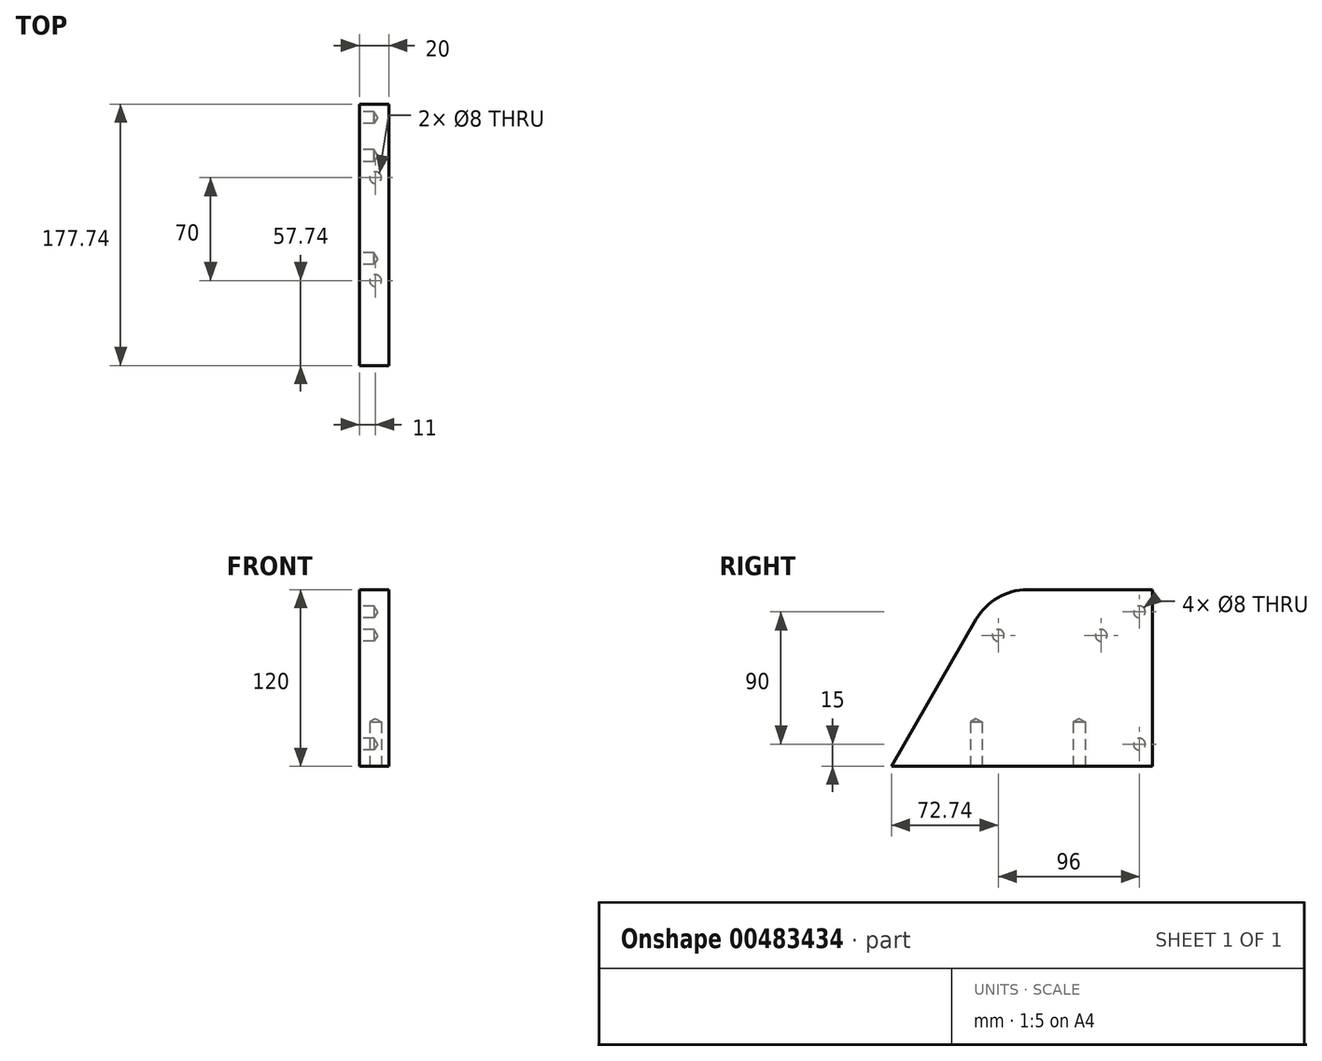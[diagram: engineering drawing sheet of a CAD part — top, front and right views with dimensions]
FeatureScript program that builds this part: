
annotation { "Feature Type Name" : "Feature", "Feature Type Description" : "" }
export const myFeature = defineFeature(function(context is Context, id is Id, definition is map)
    precondition{}
    {
        {
            var Q0;
            Q0=qCreatedBy(makeId("Right.planeOp"),FACE);
            var sketch = newSketch(context, id + "F0", { "sketchPlane" : qUnion([Q0])});
            skLineSegment(sketch, "E0", {"start": v(0, 0) * mm, "end": v(-177.74, 0) * mm});
            skLineSegment(sketch, "E1", {"start": v(-177.74, 0) * mm, "end": v(-120, 100) * mm});
            skLineSegment(sketch, "E2", {"start": v(-108.45, 120) * mm, "end": v(0, 120) * mm});
            skPoint(sketch, "E3", {"position": v(0, 100) * mm});
            skLineSegment(sketch, "E4", {"start": v(0, 100) * mm, "end": v(0, 120) * mm});
            skLineSegment(sketch, "E5", {"start": v(0, 100) * mm, "end": v(0, 0) * mm});
            skLineSegment(sketch, "E6", {"start": v(-120, 100) * mm, "end": v(-108.45, 120) * mm});
            skLineSegment(sketch, "E7", {"start": v(0, 100) * mm, "end": v(-120, 100) * mm});
            skSolve(sketch);
        }
        {
            var Q0;
            Q0=qSketchRegion(id+"F0",true);
            extrude(context, id + "F1", {"entities" : qUnion([Q0]), "depth" : 20 * mm});
        }
        {
            var Q0;
            Q0=makeQuery(id+"F1.opExtrude","SWEPT_EDGE",EDGE,{"disambiguationData":[OSD([sQuery(id+"F0.wireOp",EDGE,"E2"),sQuery(id+"F0.wireOp",EDGE,"E6")])]});
            fillet(context, id + "F2", {"entities" : qUnion([Q0]), "radius" : 40 * mm, "tangentPropagation" : true, "allowEdgeOverflow" : false});
        }
        {
            var Q0;
            Q0=makeQuery(id+"F1.opExtrude","CAP_FACE",FACE,{"disambiguationData":[OSD([sQuery(id+"F0.wireOp",EDGE,"E0"),sQuery(id+"F0.wireOp",EDGE,"E1"),sQuery(id+"F0.wireOp",EDGE,"E2"),sQuery(id+"F0.wireOp",EDGE,"E4"),sQuery(id+"F0.wireOp",EDGE,"E5"),sQuery(id+"F0.wireOp",EDGE,"E6")])],"isStart":true});
            var sketch = newSketch(context, id + "F3", { "sketchPlane" : qUnion([Q0])});
            skPoint(sketch, "E8", {"position": v(35, 89) * mm});
            skPoint(sketch, "E9", {"position": v(105, 89) * mm});
            skPoint(sketch, "E10", {"position": v(9, 15) * mm});
            skPoint(sketch, "E11", {"position": v(9, 105) * mm});
            skSolve(sketch);
        }
        {
            var Q0;
            Q0=makeQuery(id+"F1.opExtrude","SWEPT_FACE",FACE,{"disambiguationData":[OSD([sQuery(id+"F0.wireOp",EDGE,"E0")])]});
            var sketch = newSketch(context, id + "F4", { "sketchPlane" : qUnion([Q0])});
            skPoint(sketch, "E12", {"position": v(11, 50) * mm});
            skPoint(sketch, "E13", {"position": v(11, 120) * mm});
            skSolve(sketch);
        }
        {
            var Q0;
            Q0=sQuery(id+"F3.wireOp",VERTEX,"E8");
            var Q1;
            Q1=sQuery(id+"F3.wireOp",VERTEX,"E9");
            var Q2;
            Q2=sQuery(id+"F3.wireOp",VERTEX,"E10");
            var Q3;
            Q3=sQuery(id+"F3.wireOp",VERTEX,"E11");
            var Q4;
            Q4=makeQuery(id+"F1.opExtrude","SWEPT_BODY",BODY,{"disambiguationData":[OSD([sQuery(id+"F0.wireOp",EDGE,"E0"),sQuery(id+"F0.wireOp",EDGE,"E1"),sQuery(id+"F0.wireOp",EDGE,"E2"),sQuery(id+"F0.wireOp",EDGE,"E4"),sQuery(id+"F0.wireOp",EDGE,"E5"),sQuery(id+"F0.wireOp",EDGE,"E6")])]});
            hole(context, id + "F5", {"style" : HoleStyle.SIMPLE, "endStyle" : HoleEndStyle.BLIND, "standardTappedOrClearance" : lookupTablePath({ "standard" : "ISO", "size" : "8", "type" : "Drilled" }), "standardBlindInLast" : lookupTablePath({ "standard" : "ISO", "size" : "8", "type" : "Drilled" }), "holeDiameter" : 8 * mm, "holeDepth" : 10 * mm, "isTappedThrough" : true, "tappedDepth" : 12 * mm, "tapClearance" : 3, "locations" : qUnion([Q0, Q1, Q2, Q3]), "scope" : qUnion([Q4])});
        }
        {
            var Q0;
            Q0=sQuery(id+"F4.wireOp",VERTEX,"E13");
            var Q1;
            Q1=sQuery(id+"F4.wireOp",VERTEX,"E12");
            var Q2;
            Q2=makeQuery(id+"F1.opExtrude","SWEPT_BODY",BODY,{"disambiguationData":[OSD([sQuery(id+"F0.wireOp",EDGE,"E0"),sQuery(id+"F0.wireOp",EDGE,"E1"),sQuery(id+"F0.wireOp",EDGE,"E2"),sQuery(id+"F0.wireOp",EDGE,"E4"),sQuery(id+"F0.wireOp",EDGE,"E5"),sQuery(id+"F0.wireOp",EDGE,"E6")])]});
            hole(context, id + "F6", {"style" : HoleStyle.SIMPLE, "endStyle" : HoleEndStyle.BLIND, "standardTappedOrClearance" : lookupTablePath({ "standard" : "ISO", "size" : "8", "type" : "Drilled" }), "standardBlindInLast" : lookupTablePath({ "standard" : "ISO", "size" : "8", "type" : "Drilled" }), "holeDiameter" : 8 * mm, "holeDepth" : 30 * mm, "isTappedThrough" : true, "tappedDepth" : 12 * mm, "tapClearance" : 3, "locations" : qUnion([Q0, Q1]), "scope" : qUnion([Q2])});
        }
    });
